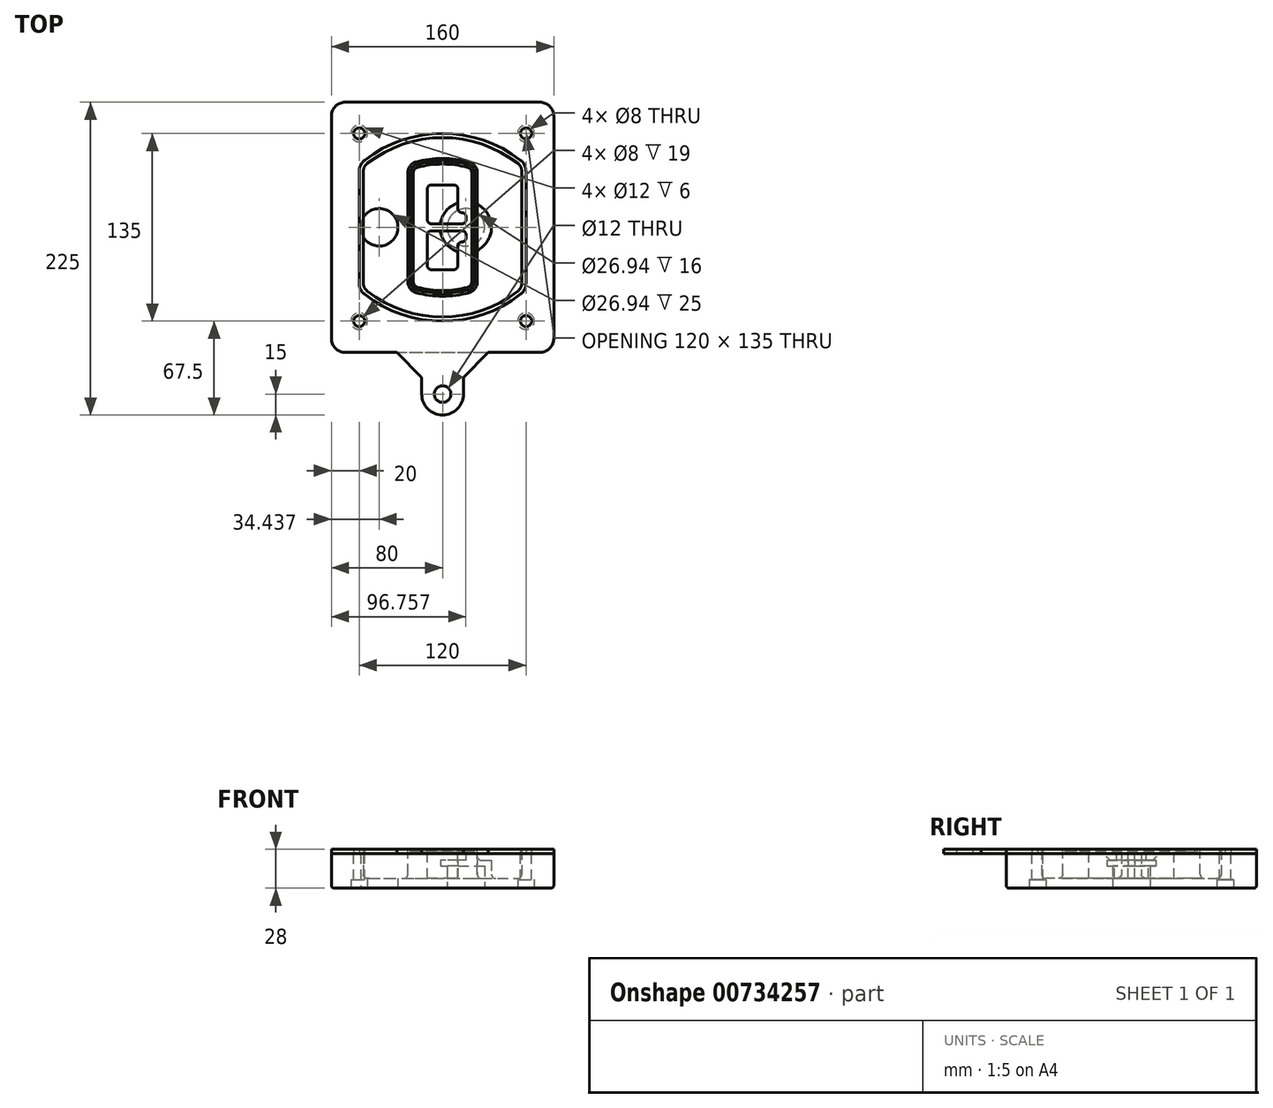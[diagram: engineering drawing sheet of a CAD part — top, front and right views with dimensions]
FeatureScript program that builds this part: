
annotation { "Feature Type Name" : "Feature", "Feature Type Description" : "" }
export const myFeature = defineFeature(function(context is Context, id is Id, definition is map)
    precondition{}
    {
        {
            var Q0;
            Q0=qCreatedBy(makeId("Top.planeOp"),FACE);
            var sketch = newSketch(context, id + "F0", { "sketchPlane" : qUnion([Q0])});
            skPoint(sketch, "E0.rect.middle", {"position": v(0, 0) * mm});
            skLineSegment(sketch, "E1.bottom", {"start": v(-70, -90) * mm, "end": v(70, -90) * mm});
            skLineSegment(sketch, "E1.top", {"start": v(-70, 90) * mm, "end": v(70, 90) * mm});
            skLineSegment(sketch, "E1.left", {"start": v(-80, -80) * mm, "end": v(-80, 80) * mm});
            skLineSegment(sketch, "E1.right", {"start": v(80, -80) * mm, "end": v(80, 80) * mm});
            skLineSegment(sketch, "E2", {"start": v(-80, 90) * mm, "end": v(80, -90) * mm, "construction": true});
            skLineSegment(sketch, "E3", {"start": v(80, 90) * mm, "end": v(-80, -90) * mm, "construction": true});
            skCircle(sketch, "E4", {"center": v(-60, 67.5) * mm, "radius": 4 * mm});
            skCircle(sketch, "E5", {"center": v(60, 67.5) * mm, "radius": 4 * mm});
            skCircle(sketch, "E6", {"center": v(60, -67.5) * mm, "radius": 4 * mm});
            skCircle(sketch, "E7", {"center": v(-60, -67.5) * mm, "radius": 4 * mm});
            skLineSegment(sketch, "E8", {"start": v(-60, 67.5) * mm, "end": v(60, 67.5) * mm, "construction": true});
            skLineSegment(sketch, "E9", {"start": v(60, 67.5) * mm, "end": v(60, -67.5) * mm, "construction": true});
            skLineSegment(sketch, "E10", {"start": v(60, -67.5) * mm, "end": v(-60, -67.5) * mm, "construction": true});
            skLineSegment(sketch, "E11", {"start": v(-60, -67.5) * mm, "end": v(-60, 67.5) * mm, "construction": true});
            skLineSegment(sketch, "E12", {"start": v(-60, 40.3) * mm, "end": v(-60, -40.3) * mm});
            skLineSegment(sketch, "E13", {"start": v(60, 40.3) * mm, "end": v(60, -40.3) * mm});
            skArc(sketch, "E14", {"start": v(56.15, 48.18) * mm, "mid": v(0, 67.5) * mm, "end": v(-56.15, 48.18) * mm});
            skArc(sketch, "E15", {"start": v(-56.15, -48.18) * mm, "mid": v(0, -67.5) * mm, "end": v(56.15, -48.18) * mm});
            skLineSegment(sketch, "E16", {"start": v(-60, 0) * mm, "end": v(60, 0) * mm, "construction": true});
            skPoint(sketch, "E17.visualSharp", {"position": v(-60, -45) * mm});
            skArc(sketch, "E17.filletArc", {"start": v(-60, -40.3) * mm, "mid": v(-58.99, -44.68) * mm, "end": v(-56.15, -48.18) * mm});
            skPoint(sketch, "E18.visualSharp", {"position": v(-60, 45) * mm});
            skArc(sketch, "E18.filletArc", {"start": v(-56.15, 48.18) * mm, "mid": v(-58.99, 44.68) * mm, "end": v(-60, 40.3) * mm});
            skPoint(sketch, "E19.visualSharp", {"position": v(60, 45) * mm});
            skArc(sketch, "E19.filletArc", {"start": v(60, 40.3) * mm, "mid": v(58.99, 44.68) * mm, "end": v(56.15, 48.18) * mm});
            skPoint(sketch, "E20.visualSharp", {"position": v(60, -45) * mm});
            skArc(sketch, "E20.filletArc", {"start": v(56.15, -48.18) * mm, "mid": v(58.99, -44.68) * mm, "end": v(60, -40.3) * mm});
            skPoint(sketch, "E21.visualSharp", {"position": v(-80, 90) * mm});
            skArc(sketch, "E21.filletArc", {"start": v(-70, 90) * mm, "mid": v(-77.07, 87.07) * mm, "end": v(-80, 80) * mm});
            skPoint(sketch, "E22.visualSharp", {"position": v(80, 90) * mm});
            skArc(sketch, "E22.filletArc", {"start": v(80, 80) * mm, "mid": v(77.07, 87.07) * mm, "end": v(70, 90) * mm});
            skPoint(sketch, "E23.visualSharp", {"position": v(80, -90) * mm});
            skArc(sketch, "E23.filletArc", {"start": v(70, -90) * mm, "mid": v(77.07, -87.07) * mm, "end": v(80, -80) * mm});
            skPoint(sketch, "E24.visualSharp", {"position": v(-80, -90) * mm});
            skArc(sketch, "E24.filletArc", {"start": v(-80, -80) * mm, "mid": v(-77.07, -87.07) * mm, "end": v(-70, -90) * mm});
            skArc(sketch, "E25.0", {"start": v(57, 40.3) * mm, "mid": v(56.3, 43.36) * mm, "end": v(54.3, 45.81) * mm});
            skLineSegment(sketch, "E25.1", {"start": v(57, 40.3) * mm, "end": v(57, -40.3) * mm});
            skArc(sketch, "E25.2", {"start": v(54.3, -45.81) * mm, "mid": v(56.3, -43.36) * mm, "end": v(57, -40.3) * mm});
            skArc(sketch, "E25.3", {"start": v(-54.3, -45.81) * mm, "mid": v(0, -64.5) * mm, "end": v(54.3, -45.81) * mm});
            skArc(sketch, "E25.4", {"start": v(-57, -40.3) * mm, "mid": v(-56.3, -43.36) * mm, "end": v(-54.3, -45.81) * mm});
            skArc(sketch, "E25.5", {"start": v(54.3, 45.81) * mm, "mid": v(0, 64.5) * mm, "end": v(-54.3, 45.81) * mm});
            skLineSegment(sketch, "E25.6", {"start": v(-57, 40.3) * mm, "end": v(-57, -40.3) * mm});
            skArc(sketch, "E25.7", {"start": v(-54.3, 45.81) * mm, "mid": v(-56.3, 43.36) * mm, "end": v(-57, 40.3) * mm});
            skArc(sketch, "E26.0", {"start": v(-58.62, 51.33) * mm, "mid": v(-62.58, 46.43) * mm, "end": v(-64, 40.3) * mm});
            skArc(sketch, "E26.1", {"start": v(58.62, 51.33) * mm, "mid": v(0, 71.5) * mm, "end": v(-58.62, 51.33) * mm});
            skArc(sketch, "E26.2", {"start": v(64, 40.3) * mm, "mid": v(62.58, 46.43) * mm, "end": v(58.62, 51.33) * mm});
            skLineSegment(sketch, "E26.3", {"start": v(64, 40.3) * mm, "end": v(64, -40.3) * mm});
            skArc(sketch, "E26.4", {"start": v(58.62, -51.33) * mm, "mid": v(62.58, -46.43) * mm, "end": v(64, -40.3) * mm});
            skLineSegment(sketch, "E26.5", {"start": v(-64, 40.3) * mm, "end": v(-64, -40.3) * mm});
            skArc(sketch, "E26.6", {"start": v(-58.62, -51.33) * mm, "mid": v(0, -71.5) * mm, "end": v(58.62, -51.33) * mm});
            skArc(sketch, "E26.7", {"start": v(-64, -40.3) * mm, "mid": v(-62.58, -46.43) * mm, "end": v(-58.62, -51.33) * mm});
            skSolve(sketch);
        }
        {
            var Q0;
            Q0=makeQuery(id+"F0.imprint","IMPRINT",FACE,{"disambiguationData":[TD([[makeQuery(id+"F0.imprint","IMPRINT",EDGE,{"derivedFrom":sQuery(id+"F0.wireOp",EDGE,"E1.bottom")}),1.0]])]});
            var Q1;
            Q1=makeQuery(id+"F0.imprint","IMPRINT",FACE,{"disambiguationData":[TD([[makeQuery(id+"F0.imprint","IMPRINT",EDGE,{"derivedFrom":sQuery(id+"F0.wireOp",EDGE,"E12")}),1.0]])]});
            var Q2;
            Q2=makeQuery(id+"F0.imprint","IMPRINT",FACE,{"disambiguationData":[TD([[makeQuery(id+"F0.imprint","IMPRINT",EDGE,{"derivedFrom":sQuery(id+"F0.wireOp",EDGE,"E25.0")}),1.0]])]});
            var Q3;
            Q3=makeQuery(id+"F0.imprint","IMPRINT",FACE,{"disambiguationData":[TD([[makeQuery(id+"F0.imprint","IMPRINT",EDGE,{"derivedFrom":sQuery(id+"F0.wireOp",EDGE,"E12")}),-1.0]])]});
            extrude(context, id + "F1", {"entities" : qUnion([Q0, Q1, Q2, Q3]), "oppositeDirection" : true, "depth" : 25 * mm});
        }
        {
            var Q0;
            Q0=makeQuery(id+"F0.imprint","IMPRINT",FACE,{"disambiguationData":[TD([[makeQuery(id+"F0.imprint","IMPRINT",EDGE,{"derivedFrom":sQuery(id+"F0.wireOp",EDGE,"E12")}),1.0]])]});
            extrude(context, id + "F2", {"entities" : qUnion([Q0]), "operationType" : NewBodyOperationType.ADD, "depth" : 3 * mm});
        }
        {
            var Q0;
            Q0=makeQuery(id+"F0.imprint","IMPRINT",FACE,{"disambiguationData":[TD([[makeQuery(id+"F0.imprint","IMPRINT",EDGE,{"derivedFrom":sQuery(id+"F0.wireOp",EDGE,"E25.0")}),1.0]])]});
            extrude(context, id + "F3", {"entities" : qUnion([Q0]), "operationType" : NewBodyOperationType.REMOVE, "oppositeDirection" : true, "depth" : 18 * mm});
        }
        {
            var Q0;
            Q0=makeQuery(id+"F2.opExtrude","CAP_FACE",FACE,{"disambiguationData":[OSD([sQuery(id+"F0.wireOp",EDGE,"E12"),sQuery(id+"F0.wireOp",EDGE,"E13"),sQuery(id+"F0.wireOp",EDGE,"E14"),sQuery(id+"F0.wireOp",EDGE,"E15"),sQuery(id+"F0.wireOp",EDGE,"E17.filletArc"),sQuery(id+"F0.wireOp",EDGE,"E18.filletArc"),sQuery(id+"F0.wireOp",EDGE,"E19.filletArc"),sQuery(id+"F0.wireOp",EDGE,"E20.filletArc"),sQuery(id+"F0.wireOp",EDGE,"E25.0"),sQuery(id+"F0.wireOp",EDGE,"E25.1"),sQuery(id+"F0.wireOp",EDGE,"E25.2"),sQuery(id+"F0.wireOp",EDGE,"E25.3"),sQuery(id+"F0.wireOp",EDGE,"E25.4"),sQuery(id+"F0.wireOp",EDGE,"E25.5"),sQuery(id+"F0.wireOp",EDGE,"E25.6"),sQuery(id+"F0.wireOp",EDGE,"E25.7")])],"isStart":false});
            var sketch = newSketch(context, id + "F4", { "sketchPlane" : qUnion([Q0])});
            skArc(sketch, "E27.0", {"start": v(-19.08, -46.97) * mm, "mid": v(0, -49.5) * mm, "end": v(19.08, -46.97) * mm});
            skArc(sketch, "E28.0", {"start": v(19.08, 46.97) * mm, "mid": v(0, 49.5) * mm, "end": v(-19.08, 46.97) * mm});
            skLineSegment(sketch, "E29", {"start": v(-25, 39.25) * mm, "end": v(-25, -39.25) * mm});
            skLineSegment(sketch, "E30", {"start": v(25, 39.25) * mm, "end": v(25, -39.25) * mm});
            skLineSegment(sketch, "E31", {"start": v(-25, 45.1) * mm, "end": v(25, 45.1) * mm, "construction": true});
            skLineSegment(sketch, "E32", {"start": v(-25, -45.1) * mm, "end": v(25, -45.1) * mm, "construction": true});
            skPoint(sketch, "E33.visualSharp", {"position": v(-25, 45.1) * mm});
            skArc(sketch, "E33.filletArc", {"start": v(-19.08, 46.97) * mm, "mid": v(-23.35, 44.11) * mm, "end": v(-25, 39.25) * mm});
            skPoint(sketch, "E34.visualSharp", {"position": v(25, 45.1) * mm});
            skArc(sketch, "E34.filletArc", {"start": v(25, 39.25) * mm, "mid": v(23.35, 44.11) * mm, "end": v(19.08, 46.97) * mm});
            skPoint(sketch, "E35.visualSharp", {"position": v(25, -45.1) * mm});
            skArc(sketch, "E35.filletArc", {"start": v(19.08, -46.97) * mm, "mid": v(23.35, -44.11) * mm, "end": v(25, -39.25) * mm});
            skPoint(sketch, "E36.visualSharp", {"position": v(-25, -45.1) * mm});
            skArc(sketch, "E36.filletArc", {"start": v(-25, -39.25) * mm, "mid": v(-23.35, -44.11) * mm, "end": v(-19.08, -46.97) * mm});
            skArc(sketch, "E37.0", {"start": v(54.3, 45.81) * mm, "mid": v(0, 64.5) * mm, "end": v(-54.3, 45.81) * mm});
            skArc(sketch, "E37.1", {"start": v(-54.3, 45.81) * mm, "mid": v(-56.3, 43.36) * mm, "end": v(-57, 40.3) * mm});
            skLineSegment(sketch, "E37.2", {"start": v(-57, 40.3) * mm, "end": v(-57, -40.3) * mm});
            skArc(sketch, "E37.3", {"start": v(-57, -40.3) * mm, "mid": v(-56.3, -43.36) * mm, "end": v(-54.3, -45.81) * mm});
            skArc(sketch, "E37.4", {"start": v(-54.3, -45.81) * mm, "mid": v(0, -64.5) * mm, "end": v(54.3, -45.81) * mm});
            skArc(sketch, "E37.5", {"start": v(54.3, -45.81) * mm, "mid": v(56.3, -43.36) * mm, "end": v(57, -40.3) * mm});
            skLineSegment(sketch, "E37.6", {"start": v(57, 40.3) * mm, "end": v(57, -40.3) * mm});
            skArc(sketch, "E37.7", {"start": v(57, 40.3) * mm, "mid": v(56.3, 43.36) * mm, "end": v(54.3, 45.81) * mm});
            skLineSegment(sketch, "E38.0", {"start": v(23, 39.25) * mm, "end": v(23, -39.25) * mm});
            skArc(sketch, "E38.1", {"start": v(18.56, -45.04) * mm, "mid": v(21.76, -42.9) * mm, "end": v(23, -39.25) * mm});
            skArc(sketch, "E38.2", {"start": v(-18.56, -45.04) * mm, "mid": v(0, -47.5) * mm, "end": v(18.56, -45.04) * mm});
            skArc(sketch, "E38.3", {"start": v(-23, -39.25) * mm, "mid": v(-21.76, -42.9) * mm, "end": v(-18.56, -45.04) * mm});
            skLineSegment(sketch, "E38.4", {"start": v(-23, 39.25) * mm, "end": v(-23, -39.25) * mm});
            skArc(sketch, "E38.5", {"start": v(23, 39.25) * mm, "mid": v(21.76, 42.9) * mm, "end": v(18.56, 45.04) * mm});
            skArc(sketch, "E38.6", {"start": v(-18.56, 45.04) * mm, "mid": v(-21.76, 42.9) * mm, "end": v(-23, 39.25) * mm});
            skArc(sketch, "E38.7", {"start": v(18.56, 45.04) * mm, "mid": v(0, 47.5) * mm, "end": v(-18.56, 45.04) * mm});
            skArc(sketch, "E39.0", {"start": v(21, 39.25) * mm, "mid": v(20.18, 41.68) * mm, "end": v(18.04, 43.1) * mm});
            skLineSegment(sketch, "E39.1", {"start": v(21, 39.25) * mm, "end": v(21, -39.25) * mm});
            skArc(sketch, "E39.2", {"start": v(18.04, -43.1) * mm, "mid": v(20.18, -41.68) * mm, "end": v(21, -39.25) * mm});
            skArc(sketch, "E39.3", {"start": v(-18.04, -43.1) * mm, "mid": v(0, -45.5) * mm, "end": v(18.04, -43.1) * mm});
            skArc(sketch, "E39.4", {"start": v(-21, -39.25) * mm, "mid": v(-20.18, -41.68) * mm, "end": v(-18.04, -43.1) * mm});
            skArc(sketch, "E39.5", {"start": v(18.04, 43.1) * mm, "mid": v(0, 45.5) * mm, "end": v(-18.04, 43.1) * mm});
            skLineSegment(sketch, "E39.6", {"start": v(-21, 39.25) * mm, "end": v(-21, -39.25) * mm});
            skArc(sketch, "E39.7", {"start": v(-18.04, 43.1) * mm, "mid": v(-20.18, 41.68) * mm, "end": v(-21, 39.25) * mm});
            skLineSegment(sketch, "E40", {"start": v(-25, 0) * mm, "end": v(25, 0) * mm, "construction": true});
            skLineSegment(sketch, "E41", {"start": v(-11, 5.5) * mm, "end": v(-11, 27.5) * mm});
            skLineSegment(sketch, "E42", {"start": v(-8, 30.5) * mm, "end": v(8, 30.5) * mm});
            skLineSegment(sketch, "E43", {"start": v(11, 27.5) * mm, "end": v(11, 13.5) * mm});
            skLineSegment(sketch, "E44", {"start": v(14, 10.5) * mm, "end": v(14, 10.5) * mm});
            skLineSegment(sketch, "E45", {"start": v(17, 7.5) * mm, "end": v(17, 5.5) * mm});
            skLineSegment(sketch, "E46", {"start": v(14, 2.5) * mm, "end": v(-8, 2.5) * mm});
            skPoint(sketch, "E47.visualSharp", {"position": v(-11, 30.5) * mm});
            skArc(sketch, "E47.filletArc", {"start": v(-8, 30.5) * mm, "mid": v(-10.12, 29.62) * mm, "end": v(-11, 27.5) * mm});
            skPoint(sketch, "E48.visualSharp", {"position": v(11, 30.5) * mm});
            skArc(sketch, "E48.filletArc", {"start": v(11, 27.5) * mm, "mid": v(10.12, 29.62) * mm, "end": v(8, 30.5) * mm});
            skPoint(sketch, "E49.visualSharp", {"position": v(11, 10.5) * mm});
            skArc(sketch, "E49.filletArc", {"start": v(11, 13.5) * mm, "mid": v(11.88, 11.38) * mm, "end": v(14, 10.5) * mm});
            skPoint(sketch, "E50.visualSharp", {"position": v(17, 10.5) * mm});
            skArc(sketch, "E50.filletArc", {"start": v(17, 7.5) * mm, "mid": v(16.12, 9.62) * mm, "end": v(14, 10.5) * mm});
            skPoint(sketch, "E51.visualSharp", {"position": v(17, 2.5) * mm});
            skArc(sketch, "E51.filletArc", {"start": v(14, 2.5) * mm, "mid": v(16.12, 3.38) * mm, "end": v(17, 5.5) * mm});
            skPoint(sketch, "E52.visualSharp", {"position": v(-11, 2.5) * mm});
            skArc(sketch, "E52.filletArc", {"start": v(-11, 5.5) * mm, "mid": v(-10.12, 3.38) * mm, "end": v(-8, 2.5) * mm});
            skLineSegment(sketch, "E53.0.MirrorCS", {"start": v(14, -2.5) * mm, "end": v(-8, -2.5) * mm});
            skArc(sketch, "E54.0.MirrorCS", {"start": v(-11, -5.5) * mm, "mid": v(-10.12, -3.38) * mm, "end": v(-8, -2.5) * mm});
            skLineSegment(sketch, "E55.0.MirrorCS", {"start": v(-11, -5.5) * mm, "end": v(-11, -27.5) * mm});
            skArc(sketch, "E56.0.MirrorCS", {"start": v(-8, -30.5) * mm, "mid": v(-10.12, -29.62) * mm, "end": v(-11, -27.5) * mm});
            skLineSegment(sketch, "E57.0.MirrorCS", {"start": v(-8, -30.5) * mm, "end": v(8, -30.5) * mm});
            skArc(sketch, "E58.0.MirrorCS", {"start": v(11, -27.5) * mm, "mid": v(10.12, -29.62) * mm, "end": v(8, -30.5) * mm});
            skLineSegment(sketch, "E59.0.MirrorCS", {"start": v(11, -27.5) * mm, "end": v(11, -13.5) * mm});
            skArc(sketch, "E60.0.MirrorCS", {"start": v(11, -13.5) * mm, "mid": v(11.88, -11.38) * mm, "end": v(14, -10.5) * mm});
            skArc(sketch, "E61.0.MirrorCS", {"start": v(17, -7.5) * mm, "mid": v(16.12, -9.62) * mm, "end": v(14, -10.5) * mm});
            skLineSegment(sketch, "E62.0.MirrorCS", {"start": v(17, -7.5) * mm, "end": v(17, -5.5) * mm});
            skArc(sketch, "E63.0.MirrorCS", {"start": v(14, -2.5) * mm, "mid": v(16.12, -3.38) * mm, "end": v(17, -5.5) * mm});
            skSolve(sketch);
        }
        {
            var Q0;
            Q0=makeQuery(id+"F4.imprint","IMPRINT",FACE,{"disambiguationData":[TD([[makeQuery(id+"F4.imprint","IMPRINT",EDGE,{"derivedFrom":sQuery(id+"F4.wireOp",EDGE,"E27.0")}),1.0]])]});
            var Q1;
            Q1=makeQuery(id+"F4.imprint","IMPRINT",FACE,{"disambiguationData":[TD([[makeQuery(id+"F4.imprint","IMPRINT",EDGE,{"derivedFrom":sQuery(id+"F4.wireOp",EDGE,"E38.0")}),-1.0]])]});
            var Q2;
            Q2=makeQuery(id+"F4.imprint","IMPRINT",FACE,{"disambiguationData":[TD([[makeQuery(id+"F4.imprint","IMPRINT",EDGE,{"derivedFrom":sQuery(id+"F4.wireOp",EDGE,"E39.0")}),1.0]])]});
            extrude(context, id + "F5", {"entities" : qUnion([Q0, Q1, Q2]), "operationType" : NewBodyOperationType.ADD, "endBound" : BoundingType.UP_TO_NEXT, "oppositeDirection" : true, "depth" : 25 * mm});
        }
        {
            var Q0;
            Q0=makeQuery(id+"F4.imprint","IMPRINT",FACE,{"disambiguationData":[TD([[makeQuery(id+"F4.imprint","IMPRINT",EDGE,{"derivedFrom":sQuery(id+"F4.wireOp",EDGE,"E38.0")}),-1.0]])]});
            extrude(context, id + "F6", {"entities" : qUnion([Q0]), "operationType" : NewBodyOperationType.REMOVE, "oppositeDirection" : true, "depth" : 2 * mm});
        }
        {
            var Q0;
            Q0=makeQuery(id+"F1.opExtrude","CAP_FACE",FACE,{"disambiguationData":[OSD([sQuery(id+"F0.wireOp",EDGE,"E1.bottom"),sQuery(id+"F0.wireOp",EDGE,"E1.top"),sQuery(id+"F0.wireOp",EDGE,"E1.left"),sQuery(id+"F0.wireOp",EDGE,"E1.right"),sQuery(id+"F0.wireOp",EDGE,"E4"),sQuery(id+"F0.wireOp",EDGE,"E5"),sQuery(id+"F0.wireOp",EDGE,"E6"),sQuery(id+"F0.wireOp",EDGE,"E7"),sQuery(id+"F0.wireOp",EDGE,"E21.filletArc"),sQuery(id+"F0.wireOp",EDGE,"E22.filletArc"),sQuery(id+"F0.wireOp",EDGE,"E23.filletArc"),sQuery(id+"F0.wireOp",EDGE,"E24.filletArc")])],"isStart":false});
            var sketch = newSketch(context, id + "F7", { "sketchPlane" : qUnion([Q0])});
            skCircle(sketch, "E64", {"center": v(16.76, 0) * mm, "radius": 13.47 * mm});
            skCircle(sketch, "E65", {"center": v(-45.56, 0) * mm, "radius": 13.47 * mm});
            skLineSegment(sketch, "E66", {"start": v(80, 0) * mm, "end": v(-80, 0) * mm});
            skCircle(sketch, "E67", {"center": v(16.76, 0) * mm, "radius": 18.47 * mm});
            skCircle(sketch, "E68", {"center": v(60, -67.5) * mm, "radius": 6 * mm});
            skCircle(sketch, "E69", {"center": v(-60, -67.5) * mm, "radius": 6 * mm});
            skCircle(sketch, "E70", {"center": v(-60, 67.5) * mm, "radius": 6 * mm});
            skCircle(sketch, "E71", {"center": v(60, 67.5) * mm, "radius": 6 * mm});
            skSolve(sketch);
        }
        {
            var Q0;
            {var subQ1=sQuery(id+"F7.wireOp",EDGE,"E66");var subQ4=sQuery(id+"F7.wireOp",EDGE,"E64");var subQ6=makeQuery(id+"F7.imprint","INTERSECT",VERTEX,{"disambiguationData":[OD(0.0)],"derivedFrom":[subQ4,subQ1]});Q0=makeQuery(id+"F7.imprint","IMPRINT",FACE,{"disambiguationData":[TD([[makeQuery(id+"F7.imprint","IMPRINT",EDGE,{"disambiguationData":[TD([[subQ6,-1.0]])],"derivedFrom":subQ4}),-1.0]])]});}
            var Q1;
            {var subQ0=sQuery(id+"F7.wireOp",EDGE,"E66");var subQ1=sQuery(id+"F7.wireOp",EDGE,"E64");var subQ3=makeQuery(id+"F7.imprint","INTERSECT",VERTEX,{"disambiguationData":[OD(0.0)],"derivedFrom":[subQ1,subQ0]});Q1=makeQuery(id+"F7.imprint","IMPRINT",FACE,{"disambiguationData":[TD([[makeQuery(id+"F7.imprint","IMPRINT",EDGE,{"disambiguationData":[TD([[subQ3,-1.0]])],"derivedFrom":subQ1}),1.0]])]});}
            var Q2;
            {var subQ0=sQuery(id+"F7.wireOp",EDGE,"E66");var subQ1=sQuery(id+"F7.wireOp",EDGE,"E64");var subQ3=makeQuery(id+"F7.imprint","INTERSECT",VERTEX,{"disambiguationData":[OD(0.0)],"derivedFrom":[subQ1,subQ0]});Q2=makeQuery(id+"F7.imprint","IMPRINT",FACE,{"disambiguationData":[TD([[makeQuery(id+"F7.imprint","IMPRINT",EDGE,{"disambiguationData":[TD([[subQ3,1.0]])],"derivedFrom":subQ1}),1.0]])]});}
            var Q3;
            {var subQ1=sQuery(id+"F7.wireOp",EDGE,"E66");var subQ4=sQuery(id+"F7.wireOp",EDGE,"E64");var subQ6=makeQuery(id+"F7.imprint","INTERSECT",VERTEX,{"disambiguationData":[OD(0.0)],"derivedFrom":[subQ4,subQ1]});Q3=makeQuery(id+"F7.imprint","IMPRINT",FACE,{"disambiguationData":[TD([[makeQuery(id+"F7.imprint","IMPRINT",EDGE,{"disambiguationData":[TD([[subQ6,1.0]])],"derivedFrom":subQ4}),-1.0]])]});}
            extrude(context, id + "F8", {"entities" : qUnion([Q0, Q1, Q2, Q3]), "operationType" : NewBodyOperationType.ADD, "oppositeDirection" : true, "depth" : 20 * mm});
        }
        {
            var Q0;
            {var subQ0=sQuery(id+"F7.wireOp",EDGE,"E66");var subQ1=sQuery(id+"F7.wireOp",EDGE,"E64");var subQ3=makeQuery(id+"F7.imprint","INTERSECT",VERTEX,{"disambiguationData":[OD(0.0)],"derivedFrom":[subQ1,subQ0]});Q0=makeQuery(id+"F7.imprint","IMPRINT",FACE,{"disambiguationData":[TD([[makeQuery(id+"F7.imprint","IMPRINT",EDGE,{"disambiguationData":[TD([[subQ3,-1.0]])],"derivedFrom":subQ1}),1.0]])]});}
            var Q1;
            {var subQ0=sQuery(id+"F7.wireOp",EDGE,"E66");var subQ1=sQuery(id+"F7.wireOp",EDGE,"E64");var subQ3=makeQuery(id+"F7.imprint","INTERSECT",VERTEX,{"disambiguationData":[OD(0.0)],"derivedFrom":[subQ1,subQ0]});Q1=makeQuery(id+"F7.imprint","IMPRINT",FACE,{"disambiguationData":[TD([[makeQuery(id+"F7.imprint","IMPRINT",EDGE,{"disambiguationData":[TD([[subQ3,1.0]])],"derivedFrom":subQ1}),1.0]])]});}
            extrude(context, id + "F9", {"entities" : qUnion([Q0, Q1]), "operationType" : NewBodyOperationType.REMOVE, "oppositeDirection" : true, "depth" : 16 * mm});
        }
        {
            var Q0;
            {var subQ0=sQuery(id+"F7.wireOp",EDGE,"E66");var subQ1=sQuery(id+"F7.wireOp",EDGE,"E65");var subQ3=makeQuery(id+"F7.imprint","INTERSECT",VERTEX,{"disambiguationData":[OD(0.0)],"derivedFrom":[subQ1,subQ0]});Q0=makeQuery(id+"F7.imprint","IMPRINT",FACE,{"disambiguationData":[TD([[makeQuery(id+"F7.imprint","IMPRINT",EDGE,{"disambiguationData":[TD([[subQ3,-1.0]])],"derivedFrom":subQ1}),1.0]])]});}
            var Q1;
            {var subQ0=sQuery(id+"F7.wireOp",EDGE,"E66");var subQ1=sQuery(id+"F7.wireOp",EDGE,"E65");var subQ3=makeQuery(id+"F7.imprint","INTERSECT",VERTEX,{"disambiguationData":[OD(0.0)],"derivedFrom":[subQ1,subQ0]});Q1=makeQuery(id+"F7.imprint","IMPRINT",FACE,{"disambiguationData":[TD([[makeQuery(id+"F7.imprint","IMPRINT",EDGE,{"disambiguationData":[TD([[subQ3,1.0]])],"derivedFrom":subQ1}),1.0]])]});}
            extrude(context, id + "F10", {"entities" : qUnion([Q0, Q1]), "operationType" : NewBodyOperationType.REMOVE, "oppositeDirection" : true, "depth" : 25 * mm});
        }
        {
            var Q0;
            Q0=makeQuery(id+"F7.imprint","IMPRINT",FACE,{"disambiguationData":[TD([[makeQuery(id+"F7.imprint","IMPRINT",EDGE,{"derivedFrom":sQuery(id+"F7.wireOp",EDGE,"E68")}),1.0]])]});
            var Q1;
            Q1=makeQuery(id+"F7.imprint","IMPRINT",FACE,{"disambiguationData":[TD([[makeQuery(id+"F7.imprint","IMPRINT",EDGE,{"derivedFrom":makeQuery(id+"F1.opExtrude","CAP_EDGE",EDGE,{"disambiguationData":[OSD([sQuery(id+"F0.wireOp",EDGE,"E5")])],"isStart":false})}),-1.0]])]});
            var Q2;
            Q2=makeQuery(id+"F7.imprint","IMPRINT",FACE,{"disambiguationData":[TD([[makeQuery(id+"F7.imprint","IMPRINT",EDGE,{"derivedFrom":sQuery(id+"F7.wireOp",EDGE,"E69")}),1.0]])]});
            var Q3;
            Q3=makeQuery(id+"F7.imprint","IMPRINT",FACE,{"disambiguationData":[TD([[makeQuery(id+"F7.imprint","IMPRINT",EDGE,{"derivedFrom":makeQuery(id+"F1.opExtrude","CAP_EDGE",EDGE,{"disambiguationData":[OSD([sQuery(id+"F0.wireOp",EDGE,"E4")])],"isStart":false})}),-1.0]])]});
            var Q4;
            Q4=makeQuery(id+"F7.imprint","IMPRINT",FACE,{"disambiguationData":[TD([[makeQuery(id+"F7.imprint","IMPRINT",EDGE,{"derivedFrom":sQuery(id+"F7.wireOp",EDGE,"E70")}),1.0]])]});
            var Q5;
            Q5=makeQuery(id+"F7.imprint","IMPRINT",FACE,{"disambiguationData":[TD([[makeQuery(id+"F7.imprint","IMPRINT",EDGE,{"derivedFrom":makeQuery(id+"F1.opExtrude","CAP_EDGE",EDGE,{"disambiguationData":[OSD([sQuery(id+"F0.wireOp",EDGE,"E7")])],"isStart":false})}),-1.0]])]});
            var Q6;
            Q6=makeQuery(id+"F7.imprint","IMPRINT",FACE,{"disambiguationData":[TD([[makeQuery(id+"F7.imprint","IMPRINT",EDGE,{"derivedFrom":sQuery(id+"F7.wireOp",EDGE,"E71")}),1.0]])]});
            var Q7;
            Q7=makeQuery(id+"F7.imprint","IMPRINT",FACE,{"disambiguationData":[TD([[makeQuery(id+"F7.imprint","IMPRINT",EDGE,{"derivedFrom":makeQuery(id+"F1.opExtrude","CAP_EDGE",EDGE,{"disambiguationData":[OSD([sQuery(id+"F0.wireOp",EDGE,"E6")])],"isStart":false})}),-1.0]])]});
            extrude(context, id + "F11", {"entities" : qUnion([Q0, Q1, Q2, Q3, Q4, Q5, Q6, Q7]), "operationType" : NewBodyOperationType.REMOVE, "oppositeDirection" : true, "depth" : 6 * mm});
        }
        {
            var Q0;
            Q0=makeQuery(id+"F9.boolean.opBoolean","COPY",FACE,{"derivedFrom":makeQuery(id+"F9.opExtrude","CAP_FACE",FACE,{"disambiguationData":[OSD([sQuery(id+"F7.wireOp",EDGE,"E64")])],"isStart":false})});
            var sketch = newSketch(context, id + "F12", { "sketchPlane" : qUnion([Q0])});
            skArc(sketch, "E72.0", {"start": v(11, 17.55) * mm, "mid": v(2.57, 11.82) * mm, "end": v(-1.54, 2.5) * mm});
            skArc(sketch, "E72.1", {"start": v(-1.54, -2.5) * mm, "mid": v(2.57, -11.82) * mm, "end": v(11, -17.55) * mm});
            skLineSegment(sketch, "E73", {"start": v(-1.54, -2.5) * mm, "end": v(14, -2.5) * mm});
            skLineSegment(sketch, "E74.0", {"start": v(14, 2.5) * mm, "end": v(-1.54, 2.5) * mm});
            skArc(sketch, "E74.1", {"start": v(14, 2.5) * mm, "mid": v(16.12, 3.38) * mm, "end": v(17, 5.5) * mm});
            skLineSegment(sketch, "E74.2", {"start": v(17, 7.5) * mm, "end": v(17, 5.5) * mm});
            skArc(sketch, "E74.3", {"start": v(17, 7.5) * mm, "mid": v(16.12, 9.62) * mm, "end": v(14, 10.5) * mm});
            skArc(sketch, "E74.4", {"start": v(11, 13.5) * mm, "mid": v(11.88, 11.38) * mm, "end": v(14, 10.5) * mm});
            skLineSegment(sketch, "E74.5", {"start": v(11, 17.55) * mm, "end": v(11, 13.5) * mm});
            skLineSegment(sketch, "E74.7", {"start": v(14, -2.5) * mm, "end": v(-1.54, -2.5) * mm});
            skArc(sketch, "E74.8", {"start": v(14, -2.5) * mm, "mid": v(16.12, -3.38) * mm, "end": v(17, -5.5) * mm});
            skLineSegment(sketch, "E74.9", {"start": v(17, -7.5) * mm, "end": v(17, -5.5) * mm});
            skArc(sketch, "E74.10", {"start": v(17, -7.5) * mm, "mid": v(16.12, -9.62) * mm, "end": v(14, -10.5) * mm});
            skArc(sketch, "E74.11", {"start": v(11, -13.5) * mm, "mid": v(11.88, -11.38) * mm, "end": v(14, -10.5) * mm});
            skLineSegment(sketch, "E74.12", {"start": v(11, -17.55) * mm, "end": v(11, -13.5) * mm});
            skPoint(sketch, "E75.orphan", {"position": v(11, -27.5) * mm});
            skPoint(sketch, "E76.orphan", {"position": v(-8, -2.5) * mm});
            skPoint(sketch, "E77.orphan", {"position": v(-8, 2.5) * mm});
            skPoint(sketch, "E78.orphan", {"position": v(11, 27.5) * mm});
            skSolve(sketch);
        }
        {
            var Q0;
            {var subQ7=sQuery(id+"F12.wireOp",EDGE,"E72.0");var subQ14=sQuery(id+"F12.wireOp",EDGE,"E72.1");var subQ16=sQuery(id+"F12.wireOp",EDGE,"E74.1");var subQ18=sQuery(id+"F12.wireOp",EDGE,"E74.8");Q0=qUnion([makeQuery(id+"F12.imprint","IMPRINT",FACE,{"disambiguationData":[TD([[makeQuery(id+"F12.imprint","IMPRINT",EDGE,{"derivedFrom":subQ7}),1.0]])]}),makeQuery(id+"F12.imprint","IMPRINT",FACE,{"disambiguationData":[TD([[makeQuery(id+"F12.imprint","IMPRINT",EDGE,{"derivedFrom":subQ14}),1.0]])]}),makeQuery(id+"F12.imprint","IMPRINT",FACE,{"disambiguationData":[TD([[makeQuery(id+"F12.imprint","IMPRINT",EDGE,{"derivedFrom":subQ16}),1.0]])]}),makeQuery(id+"F12.imprint","IMPRINT",FACE,{"disambiguationData":[TD([[makeQuery(id+"F12.imprint","IMPRINT",EDGE,{"derivedFrom":subQ18}),-1.0]])]})]);}
            var Q1;
            Q1=makeQuery(id+"F5.boolean.opBoolean","SPLIT",FACE,{"disambiguationData":[TD([makeQuery(id+"F5.opExtrude","SWEPT_FACE",FACE,{"disambiguationData":[OSD([sQuery(id+"F4.wireOp",EDGE,"E41")])]})])],"derivedFrom":makeQuery(id+"F3.boolean.opBoolean","COPY",FACE,{"derivedFrom":makeQuery(id+"F3.opExtrude","CAP_FACE",FACE,{"disambiguationData":[OSD([sQuery(id+"F0.wireOp",EDGE,"E25.0"),sQuery(id+"F0.wireOp",EDGE,"E25.1"),sQuery(id+"F0.wireOp",EDGE,"E25.2"),sQuery(id+"F0.wireOp",EDGE,"E25.3"),sQuery(id+"F0.wireOp",EDGE,"E25.4"),sQuery(id+"F0.wireOp",EDGE,"E25.5"),sQuery(id+"F0.wireOp",EDGE,"E25.6"),sQuery(id+"F0.wireOp",EDGE,"E25.7")])],"isStart":false})})});
            extrude(context, id + "F13", {"entities" : qUnion([Q0]), "operationType" : NewBodyOperationType.REMOVE, "endBound" : BoundingType.UP_TO_SURFACE, "endBoundEntityFace" : qUnion([Q1]), "depth" : 25 * mm});
        }
        {
            var Q0;
            Q0=makeQuery(id+"F3.boolean.opBoolean","COPY",EDGE,{"derivedFrom":makeQuery(id+"F3.opExtrude","CAP_EDGE",EDGE,{"disambiguationData":[OSD([sQuery(id+"F0.wireOp",EDGE,"E25.6")])],"isStart":false})});
            var Q1;
            Q1=makeQuery(id+"F8.boolean.opBoolean","INTERSECT",EDGE,{"derivedFrom":[makeQuery(id+"F5.opExtrude","SWEPT_FACE",FACE,{"disambiguationData":[OSD([sQuery(id+"F4.wireOp",EDGE,"E30")])]}),makeQuery(id+"F8.opExtrude","CAP_FACE",FACE,{"disambiguationData":[OSD([sQuery(id+"F7.wireOp",EDGE,"E67")])],"isStart":false})]});
            var Q2;
            Q2=makeQuery(id+"F8.boolean.opBoolean","INTERSECT",EDGE,{"disambiguationData":[OD(1.0)],"derivedFrom":[makeQuery(id+"F5.opExtrude","SWEPT_FACE",FACE,{"disambiguationData":[OSD([sQuery(id+"F4.wireOp",EDGE,"E30")])]}),makeQuery(id+"F8.opExtrude","SWEPT_FACE",FACE,{"disambiguationData":[OSD([sQuery(id+"F7.wireOp",EDGE,"E67")])]})]});
            var Q3;
            {var subQ0=sQuery(id+"F4.wireOp",EDGE,"E30");Q3=makeQuery(id+"F8.boolean.opBoolean","SPLIT",EDGE,{"disambiguationData":[TD([makeQuery(id+"F5.opExtrude","SWEPT_FACE",FACE,{"disambiguationData":[OSD([sQuery(id+"F4.wireOp",EDGE,"E35.filletArc")])]})])],"derivedFrom":makeQuery(id+"F5.opExtrude","CAP_EDGE",EDGE,{"disambiguationData":[OSD([subQ0])],"isStart":false})});}
            var Q4;
            {var subQ0=sQuery(id+"F0.wireOp",EDGE,"E25.7");var subQ1=sQuery(id+"F0.wireOp",EDGE,"E25.1");var subQ2=sQuery(id+"F0.wireOp",EDGE,"E25.6");var subQ3=sQuery(id+"F0.wireOp",EDGE,"E25.5");var subQ4=sQuery(id+"F0.wireOp",EDGE,"E25.4");var subQ5=sQuery(id+"F0.wireOp",EDGE,"E25.0");var subQ6=sQuery(id+"F0.wireOp",EDGE,"E25.2");var subQ7=sQuery(id+"F0.wireOp",EDGE,"E25.3");Q4=makeQuery(id+"F8.boolean.opBoolean","INTERSECT",EDGE,{"derivedFrom":[makeQuery(id+"F5.boolean.opBoolean","SPLIT",FACE,{"disambiguationData":[TD([makeQuery(id+"F2.opExtrude","SWEPT_FACE",FACE,{"disambiguationData":[OSD([subQ5])]})])],"derivedFrom":makeQuery(id+"F3.boolean.opBoolean","COPY",FACE,{"derivedFrom":makeQuery(id+"F3.opExtrude","CAP_FACE",FACE,{"disambiguationData":[OSD([subQ5,subQ1,subQ6,subQ7,subQ4,subQ3,subQ2,subQ0])],"isStart":false})})}),makeQuery(id+"F8.opExtrude","SWEPT_FACE",FACE,{"disambiguationData":[OSD([sQuery(id+"F7.wireOp",EDGE,"E67")])]})]});}
            var Q5;
            Q5=makeQuery(id+"F8.boolean.opBoolean","INTERSECT",EDGE,{"disambiguationData":[OD(0.0)],"derivedFrom":[makeQuery(id+"F5.opExtrude","SWEPT_FACE",FACE,{"disambiguationData":[OSD([sQuery(id+"F4.wireOp",EDGE,"E30")])]}),makeQuery(id+"F8.opExtrude","SWEPT_FACE",FACE,{"disambiguationData":[OSD([sQuery(id+"F7.wireOp",EDGE,"E67")])]})]});
            fillet(context, id + "F14", {"entities" : qUnion([Q0, Q1, Q2, Q3, Q4, Q5]), "radius" : 3 * mm, "tangentPropagation" : true, "allowEdgeOverflow" : false});
        }
        {
            var Q0;
            Q0=makeQuery(id+"F1.opExtrude","CAP_EDGE",EDGE,{"disambiguationData":[OSD([sQuery(id+"F0.wireOp",EDGE,"E1.bottom")])],"isStart":false});
            fillet(context, id + "F15", {"entities" : qUnion([Q0]), "radius" : 2 * mm, "tangentPropagation" : true, "allowEdgeOverflow" : false});
        }
        {
            var Q0;
            {var subQ0=sQuery(id+"F0.wireOp",EDGE,"E21.filletArc");var subQ1=sQuery(id+"F0.wireOp",EDGE,"E7");var subQ2=sQuery(id+"F0.wireOp",EDGE,"E6");var subQ3=sQuery(id+"F0.wireOp",EDGE,"E5");var subQ4=sQuery(id+"F0.wireOp",EDGE,"E4");var subQ5=sQuery(id+"F0.wireOp",EDGE,"E22.filletArc");var subQ6=sQuery(id+"F0.wireOp",EDGE,"E1.bottom");var subQ7=sQuery(id+"F0.wireOp",EDGE,"E1.right");var subQ8=sQuery(id+"F0.wireOp",EDGE,"E1.top");var subQ9=sQuery(id+"F0.wireOp",EDGE,"E1.left");var subQ10=sQuery(id+"F0.wireOp",EDGE,"E23.filletArc");var subQ11=sQuery(id+"F0.wireOp",EDGE,"E24.filletArc");Q0=makeQuery(id+"F2.boolean.opBoolean","SPLIT",FACE,{"disambiguationData":[TD([makeQuery(id+"F1.opExtrude","SWEPT_FACE",FACE,{"disambiguationData":[OSD([subQ6])]})])],"derivedFrom":makeQuery(id+"F1.opExtrude","CAP_FACE",FACE,{"disambiguationData":[OSD([subQ6,subQ8,subQ9,subQ7,subQ4,subQ3,subQ2,subQ1,subQ0,subQ5,subQ10,subQ11])],"isStart":true})});}
            var sketch = newSketch(context, id + "F16", { "sketchPlane" : qUnion([Q0])});
            skCircle(sketch, "E79.0", {"center": v(-60, 67.5) * mm, "radius": 4 * mm});
            skCircle(sketch, "E79.1", {"center": v(60, 67.5) * mm, "radius": 4 * mm});
            skLineSegment(sketch, "E79.2", {"start": v(60, 40.3) * mm, "end": v(60, -40.3) * mm});
            skArc(sketch, "E79.3", {"start": v(-56.15, -48.18) * mm, "mid": v(0, -67.5) * mm, "end": v(56.15, -48.18) * mm});
            skArc(sketch, "E79.4", {"start": v(56.15, -48.18) * mm, "mid": v(58.99, -44.68) * mm, "end": v(60, -40.3) * mm});
            skArc(sketch, "E79.5", {"start": v(-60, -40.3) * mm, "mid": v(-58.99, -44.68) * mm, "end": v(-56.15, -48.18) * mm});
            skLineSegment(sketch, "E79.6", {"start": v(-60, 40.3) * mm, "end": v(-60, -40.3) * mm});
            skArc(sketch, "E79.7", {"start": v(56.15, 48.18) * mm, "mid": v(0, 67.5) * mm, "end": v(-56.15, 48.18) * mm});
            skArc(sketch, "E79.8", {"start": v(60, 40.3) * mm, "mid": v(58.99, 44.68) * mm, "end": v(56.15, 48.18) * mm});
            skArc(sketch, "E79.9", {"start": v(-56.15, 48.18) * mm, "mid": v(-58.99, 44.68) * mm, "end": v(-60, 40.3) * mm});
            skLineSegment(sketch, "E79.10", {"start": v(-70, 90) * mm, "end": v(70, 90) * mm});
            skArc(sketch, "E79.11", {"start": v(-70, 90) * mm, "mid": v(-77.07, 87.07) * mm, "end": v(-80, 80) * mm});
            skLineSegment(sketch, "E79.12", {"start": v(-80, -80) * mm, "end": v(-80, 80) * mm});
            skArc(sketch, "E79.13", {"start": v(80, 80) * mm, "mid": v(77.07, 87.07) * mm, "end": v(70, 90) * mm});
            skLineSegment(sketch, "E79.14", {"start": v(80, -80) * mm, "end": v(80, 80) * mm});
            skCircle(sketch, "E79.15", {"center": v(60, -67.5) * mm, "radius": 4 * mm});
            skCircle(sketch, "E79.16", {"center": v(-60, -67.5) * mm, "radius": 4 * mm});
            skLineSegment(sketch, "E79.17", {"start": v(-70, -90) * mm, "end": v(70, -90) * mm});
            skArc(sketch, "E79.18", {"start": v(-80, -80) * mm, "mid": v(-77.07, -87.07) * mm, "end": v(-70, -90) * mm});
            skArc(sketch, "E79.19", {"start": v(70, -90) * mm, "mid": v(77.07, -87.07) * mm, "end": v(80, -80) * mm});
            skLineSegment(sketch, "E80", {"start": v(0, 90) * mm, "end": v(-33, 90) * mm});
            skLineSegment(sketch, "E81", {"start": v(0, 90) * mm, "end": v(33, 90) * mm});
            skLineSegment(sketch, "E82", {"start": v(-33, 90) * mm, "end": v(-15, 108) * mm});
            skLineSegment(sketch, "E83", {"start": v(33, 90) * mm, "end": v(15, 108) * mm});
            skLineSegment(sketch, "E84", {"start": v(-15, 108) * mm, "end": v(-15, 120) * mm});
            skLineSegment(sketch, "E85", {"start": v(15, 108) * mm, "end": v(15, 120) * mm});
            skArc(sketch, "E86", {"start": v(15, 120) * mm, "mid": v(0, 135) * mm, "end": v(-15, 120) * mm});
            skCircle(sketch, "E87", {"center": v(0, 120) * mm, "radius": 6 * mm});
            skLineSegment(sketch, "E88", {"start": v(0, 90) * mm, "end": v(0, 120) * mm, "construction": true});
            skLineSegment(sketch, "E89", {"start": v(-80, 0) * mm, "end": v(80, 0) * mm, "construction": true});
            skLineSegment(sketch, "E90.MirrorCS", {"start": v(-33, -90) * mm, "end": v(-15, -108) * mm});
            skLineSegment(sketch, "E91.MirrorCS", {"start": v(33, -90) * mm, "end": v(15, -108) * mm});
            skLineSegment(sketch, "E92.MirrorCS", {"start": v(0, -90) * mm, "end": v(0, -120) * mm, "construction": true});
            skLineSegment(sketch, "E93.MirrorCS", {"start": v(15, -108) * mm, "end": v(15, -120) * mm});
            skLineSegment(sketch, "E94.MirrorCS", {"start": v(-15, -108) * mm, "end": v(-15, -120) * mm});
            skCircle(sketch, "E95.MirrorC", {"center": v(0, -120) * mm, "radius": 6 * mm});
            skArc(sketch, "E96.MirrorCS", {"start": v(15, -120) * mm, "mid": v(0, -135) * mm, "end": v(-15, -120) * mm});
            skSolve(sketch);
        }
        {
            var Q0;
            Q0=makeQuery(id+"F16.imprint","IMPRINT",FACE,{"disambiguationData":[TD([[makeQuery(id+"F16.imprint","IMPRINT",EDGE,{"derivedFrom":sQuery(id+"F16.wireOp",EDGE,"E80")}),1.0]])]});
            var Q1;
            {var subQ1=sQuery(id+"F16.wireOp",EDGE,"E90.MirrorCS");Q1=makeQuery(id+"F16.imprint","IMPRINT",FACE,{"disambiguationData":[TD([[makeQuery(id+"F16.imprint","IMPRINT",EDGE,{"derivedFrom":subQ1}),1.0]])]});}
            var Q2;
            Q2=makeQuery(id+"F16.imprint","IMPRINT",FACE,{"disambiguationData":[TD([[makeQuery(id+"F16.imprint","IMPRINT",EDGE,{"derivedFrom":sQuery(id+"F16.wireOp",EDGE,"E79.0")}),-1.0]])]});
            var Q3;
            Q3=makeQuery(id+"F2.opExtrude","CAP_FACE",FACE,{"disambiguationData":[OSD([sQuery(id+"F0.wireOp",EDGE,"E12"),sQuery(id+"F0.wireOp",EDGE,"E13"),sQuery(id+"F0.wireOp",EDGE,"E14"),sQuery(id+"F0.wireOp",EDGE,"E15"),sQuery(id+"F0.wireOp",EDGE,"E17.filletArc"),sQuery(id+"F0.wireOp",EDGE,"E18.filletArc"),sQuery(id+"F0.wireOp",EDGE,"E19.filletArc"),sQuery(id+"F0.wireOp",EDGE,"E20.filletArc"),sQuery(id+"F0.wireOp",EDGE,"E25.0"),sQuery(id+"F0.wireOp",EDGE,"E25.1"),sQuery(id+"F0.wireOp",EDGE,"E25.2"),sQuery(id+"F0.wireOp",EDGE,"E25.3"),sQuery(id+"F0.wireOp",EDGE,"E25.4"),sQuery(id+"F0.wireOp",EDGE,"E25.5"),sQuery(id+"F0.wireOp",EDGE,"E25.6"),sQuery(id+"F0.wireOp",EDGE,"E25.7")])],"isStart":false});
            extrude(context, id + "F17", {"entities" : qUnion([Q0, Q1, Q2]), "endBound" : BoundingType.UP_TO_SURFACE, "depth" : 25 * mm, "endBoundEntityFace" : qUnion([Q3]), "offsetDistance" : 25 * mm});
        }
    });
